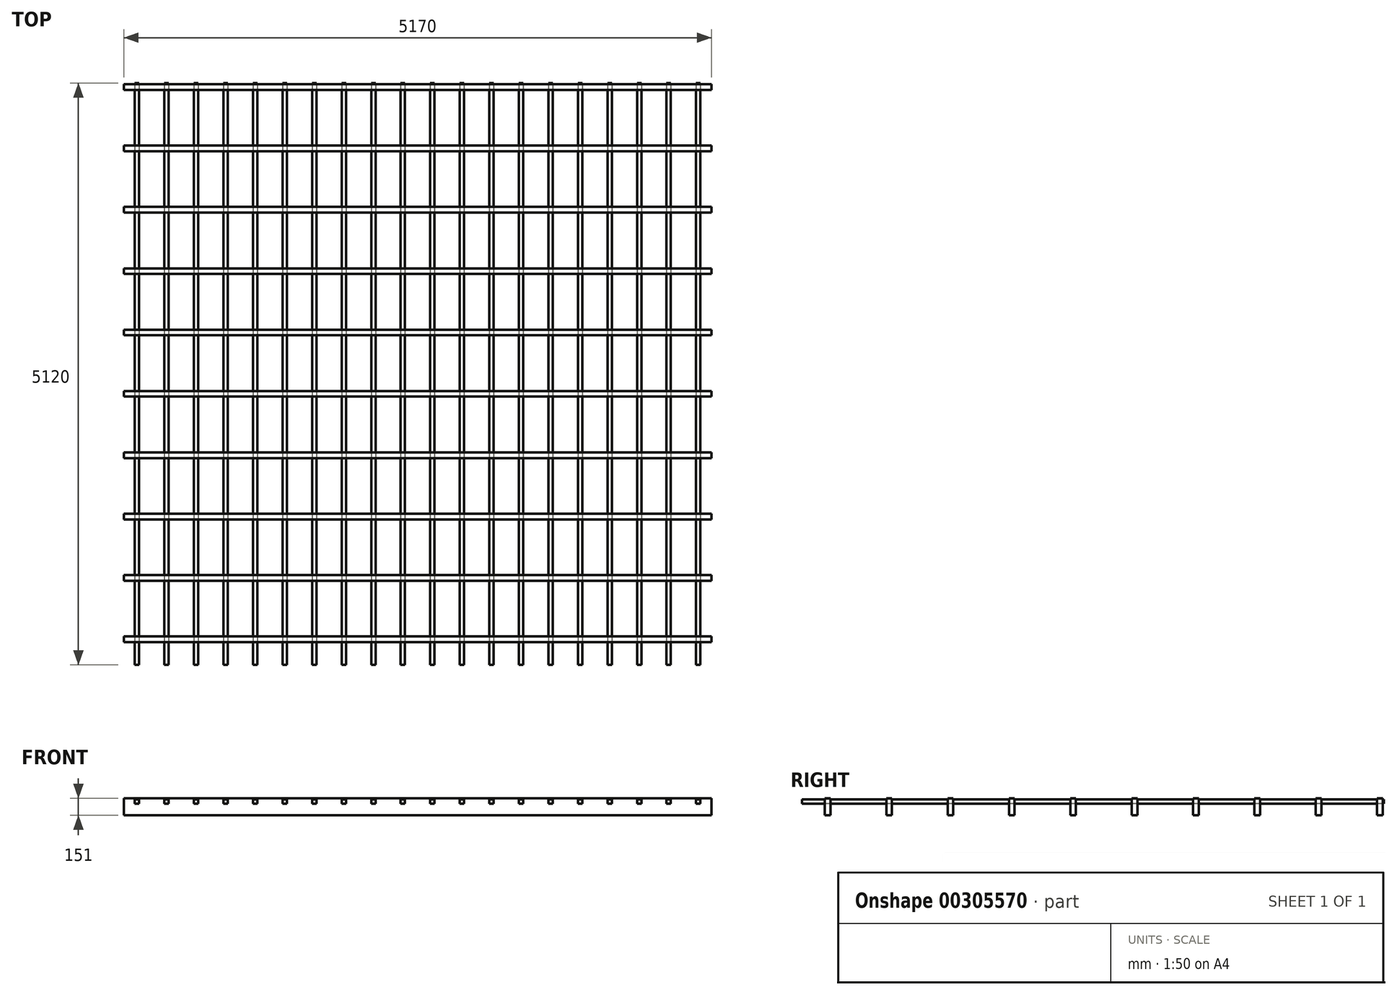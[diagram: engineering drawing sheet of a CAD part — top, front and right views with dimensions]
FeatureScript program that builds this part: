
annotation { "Feature Type Name" : "Feature", "Feature Type Description" : "" }
export const myFeature = defineFeature(function(context is Context, id is Id, definition is map)
    precondition{}
    {
        {
            var Q0;
            Q0=qCreatedBy(makeId("Top.planeOp"),FACE);
            var sketch = newSketch(context, id + "F0", { "sketchPlane" : qUnion([Q0])});
            skLineSegment(sketch, "E0.bottom", {"start": v(2585, -2460) * mm, "end": v(-2585, -2460) * mm});
            skLineSegment(sketch, "E0.top", {"start": v(2585, 2460) * mm, "end": v(-2585, 2460) * mm});
            skLineSegment(sketch, "E0.left", {"start": v(2585, -2460) * mm, "end": v(2585, 2460) * mm});
            skLineSegment(sketch, "E0.right", {"start": v(-2585, -2460) * mm, "end": v(-2585, 2460) * mm});
            skPoint(sketch, "E0.middle", {"position": v(0, 0) * mm});
            skLineSegment(sketch, "E1", {"start": v(-2585, -2410) * mm, "end": v(2585, -2410) * mm});
            skLineSegment(sketch, "E2.0.1.0", {"start": v(2585, -1920) * mm, "end": v(-2585, -1920) * mm});
            skLineSegment(sketch, "E2.0.1.1", {"start": v(-2585, -1870) * mm, "end": v(2585, -1870) * mm});
            skLineSegment(sketch, "E2.0.2.0", {"start": v(2585, -1380) * mm, "end": v(-2585, -1380) * mm});
            skLineSegment(sketch, "E2.0.2.1", {"start": v(-2585, -1330) * mm, "end": v(2585, -1330) * mm});
            skLineSegment(sketch, "E2.0.3.0", {"start": v(2585, -840) * mm, "end": v(-2585, -840) * mm});
            skLineSegment(sketch, "E2.0.3.1", {"start": v(-2585, -790) * mm, "end": v(2585, -790) * mm});
            skLineSegment(sketch, "E2.0.4.0", {"start": v(2585, -300) * mm, "end": v(-2585, -300) * mm});
            skLineSegment(sketch, "E2.0.4.1", {"start": v(-2585, -250) * mm, "end": v(2585, -250) * mm});
            skLineSegment(sketch, "E2.0.5.0", {"start": v(2585, 240) * mm, "end": v(-2585, 240) * mm});
            skLineSegment(sketch, "E2.0.5.1", {"start": v(-2585, 290) * mm, "end": v(2585, 290) * mm});
            skLineSegment(sketch, "E2.0.6.0", {"start": v(2585, 780) * mm, "end": v(-2585, 780) * mm});
            skLineSegment(sketch, "E2.0.6.1", {"start": v(-2585, 830) * mm, "end": v(2585, 830) * mm});
            skLineSegment(sketch, "E2.0.7.0", {"start": v(2585, 1320) * mm, "end": v(-2585, 1320) * mm});
            skLineSegment(sketch, "E2.0.7.1", {"start": v(-2585, 1370) * mm, "end": v(2585, 1370) * mm});
            skLineSegment(sketch, "E2.0.8.0", {"start": v(2585, 1860) * mm, "end": v(-2585, 1860) * mm});
            skLineSegment(sketch, "E2.0.8.1", {"start": v(-2585, 1910) * mm, "end": v(2585, 1910) * mm});
            skLineSegment(sketch, "E2.0.9.0", {"start": v(2585, 2400) * mm, "end": v(-2585, 2400) * mm});
            skLineSegment(sketch, "E2.0.9.1", {"start": v(-2585, 2450) * mm, "end": v(2585, 2450) * mm});
            skLineSegment(sketch, "E2.1.0.0", {"start": v(2610, -2460) * mm, "end": v(-2560, -2460) * mm});
            skLineSegment(sketch, "E2.1.0.1", {"start": v(-2560, -2410) * mm, "end": v(2610, -2410) * mm});
            skLineSegment(sketch, "E2.1.1.0", {"start": v(2610, -1920) * mm, "end": v(-2560, -1920) * mm});
            skLineSegment(sketch, "E2.1.1.1", {"start": v(-2560, -1870) * mm, "end": v(2610, -1870) * mm});
            skLineSegment(sketch, "E2.1.2.0", {"start": v(2610, -1380) * mm, "end": v(-2560, -1380) * mm});
            skLineSegment(sketch, "E2.1.2.1", {"start": v(-2560, -1330) * mm, "end": v(2610, -1330) * mm});
            skLineSegment(sketch, "E2.1.3.0", {"start": v(2610, -840) * mm, "end": v(-2560, -840) * mm});
            skLineSegment(sketch, "E2.1.3.1", {"start": v(-2560, -790) * mm, "end": v(2610, -790) * mm});
            skLineSegment(sketch, "E2.1.4.0", {"start": v(2610, -300) * mm, "end": v(-2560, -300) * mm});
            skLineSegment(sketch, "E2.1.4.1", {"start": v(-2560, -250) * mm, "end": v(2610, -250) * mm});
            skLineSegment(sketch, "E2.1.5.0", {"start": v(2610, 240) * mm, "end": v(-2560, 240) * mm});
            skLineSegment(sketch, "E2.1.5.1", {"start": v(-2560, 290) * mm, "end": v(2610, 290) * mm});
            skLineSegment(sketch, "E2.1.6.0", {"start": v(2610, 780) * mm, "end": v(-2560, 780) * mm});
            skLineSegment(sketch, "E2.1.6.1", {"start": v(-2560, 830) * mm, "end": v(2610, 830) * mm});
            skLineSegment(sketch, "E2.1.7.0", {"start": v(2610, 1320) * mm, "end": v(-2560, 1320) * mm});
            skLineSegment(sketch, "E2.1.7.1", {"start": v(-2560, 1370) * mm, "end": v(2610, 1370) * mm});
            skLineSegment(sketch, "E2.1.8.0", {"start": v(2610, 1860) * mm, "end": v(-2560, 1860) * mm});
            skLineSegment(sketch, "E2.1.8.1", {"start": v(-2560, 1910) * mm, "end": v(2610, 1910) * mm});
            skLineSegment(sketch, "E2.1.9.0", {"start": v(2610, 2400) * mm, "end": v(-2560, 2400) * mm});
            skLineSegment(sketch, "E2.1.9.1", {"start": v(-2560, 2450) * mm, "end": v(2610, 2450) * mm});
            skLineSegment(sketch, "E2.2.0.0", {"start": v(2635, -2460) * mm, "end": v(-2535, -2460) * mm});
            skLineSegment(sketch, "E2.2.0.1", {"start": v(-2535, -2410) * mm, "end": v(2635, -2410) * mm});
            skLineSegment(sketch, "E2.2.1.0", {"start": v(2635, -1920) * mm, "end": v(-2535, -1920) * mm});
            skLineSegment(sketch, "E2.2.1.1", {"start": v(-2535, -1870) * mm, "end": v(2635, -1870) * mm});
            skLineSegment(sketch, "E2.2.2.0", {"start": v(2635, -1380) * mm, "end": v(-2535, -1380) * mm});
            skLineSegment(sketch, "E2.2.2.1", {"start": v(-2535, -1330) * mm, "end": v(2635, -1330) * mm});
            skLineSegment(sketch, "E2.2.3.0", {"start": v(2635, -840) * mm, "end": v(-2535, -840) * mm});
            skLineSegment(sketch, "E2.2.3.1", {"start": v(-2535, -790) * mm, "end": v(2635, -790) * mm});
            skLineSegment(sketch, "E2.2.4.0", {"start": v(2635, -300) * mm, "end": v(-2535, -300) * mm});
            skLineSegment(sketch, "E2.2.4.1", {"start": v(-2535, -250) * mm, "end": v(2635, -250) * mm});
            skLineSegment(sketch, "E2.2.5.0", {"start": v(2635, 240) * mm, "end": v(-2535, 240) * mm});
            skLineSegment(sketch, "E2.2.5.1", {"start": v(-2535, 290) * mm, "end": v(2635, 290) * mm});
            skLineSegment(sketch, "E2.2.6.0", {"start": v(2635, 780) * mm, "end": v(-2535, 780) * mm});
            skLineSegment(sketch, "E2.2.6.1", {"start": v(-2535, 830) * mm, "end": v(2635, 830) * mm});
            skLineSegment(sketch, "E2.2.7.0", {"start": v(2635, 1320) * mm, "end": v(-2535, 1320) * mm});
            skLineSegment(sketch, "E2.2.7.1", {"start": v(-2535, 1370) * mm, "end": v(2635, 1370) * mm});
            skLineSegment(sketch, "E2.2.8.0", {"start": v(2635, 1860) * mm, "end": v(-2535, 1860) * mm});
            skLineSegment(sketch, "E2.2.8.1", {"start": v(-2535, 1910) * mm, "end": v(2635, 1910) * mm});
            skLineSegment(sketch, "E2.2.9.0", {"start": v(2635, 2400) * mm, "end": v(-2535, 2400) * mm});
            skLineSegment(sketch, "E2.2.9.1", {"start": v(-2535, 2450) * mm, "end": v(2635, 2450) * mm});
            skLineSegment(sketch, "E2.direction1", {"start": v(-2585, -2460) * mm, "end": v(-2560, -2460) * mm, "construction": true});
            skLineSegment(sketch, "E2.direction2", {"start": v(-2585, -2460) * mm, "end": v(-2585, -1920) * mm, "construction": true});
            skSolve(sketch);
        }
        {
            var Q0;
            {var subQ2=sQuery(id+"F0.wireOp",EDGE,"E0.bottom");Q0=makeQuery(id+"F0.imprint","IMPRINT",FACE,{"disambiguationData":[TD([[makeQuery(id+"F0.imprint","IMPRINT",EDGE,{"derivedFrom":subQ2}),-1.0]])]});}
            var Q1;
            {var subQ0=sQuery(id+"F0.wireOp",EDGE,"E2.0.1.0");Q1=makeQuery(id+"F0.imprint","IMPRINT",FACE,{"disambiguationData":[TD([[makeQuery(id+"F0.imprint","IMPRINT",EDGE,{"derivedFrom":subQ0}),-1.0]])]});}
            var Q2;
            {var subQ0=sQuery(id+"F0.wireOp",EDGE,"E2.0.2.0");Q2=makeQuery(id+"F0.imprint","IMPRINT",FACE,{"disambiguationData":[TD([[makeQuery(id+"F0.imprint","IMPRINT",EDGE,{"derivedFrom":subQ0}),-1.0]])]});}
            var Q3;
            {var subQ0=sQuery(id+"F0.wireOp",EDGE,"E2.0.3.0");Q3=makeQuery(id+"F0.imprint","IMPRINT",FACE,{"disambiguationData":[TD([[makeQuery(id+"F0.imprint","IMPRINT",EDGE,{"derivedFrom":subQ0}),-1.0]])]});}
            var Q4;
            {var subQ0=sQuery(id+"F0.wireOp",EDGE,"E2.0.4.0");Q4=makeQuery(id+"F0.imprint","IMPRINT",FACE,{"disambiguationData":[TD([[makeQuery(id+"F0.imprint","IMPRINT",EDGE,{"derivedFrom":subQ0}),-1.0]])]});}
            var Q5;
            {var subQ0=sQuery(id+"F0.wireOp",EDGE,"E2.0.5.0");Q5=makeQuery(id+"F0.imprint","IMPRINT",FACE,{"disambiguationData":[TD([[makeQuery(id+"F0.imprint","IMPRINT",EDGE,{"derivedFrom":subQ0}),-1.0]])]});}
            var Q6;
            {var subQ0=sQuery(id+"F0.wireOp",EDGE,"E2.0.6.0");Q6=makeQuery(id+"F0.imprint","IMPRINT",FACE,{"disambiguationData":[TD([[makeQuery(id+"F0.imprint","IMPRINT",EDGE,{"derivedFrom":subQ0}),-1.0]])]});}
            var Q7;
            {var subQ0=sQuery(id+"F0.wireOp",EDGE,"E2.0.7.0");Q7=makeQuery(id+"F0.imprint","IMPRINT",FACE,{"disambiguationData":[TD([[makeQuery(id+"F0.imprint","IMPRINT",EDGE,{"derivedFrom":subQ0}),-1.0]])]});}
            var Q8;
            {var subQ0=sQuery(id+"F0.wireOp",EDGE,"E2.0.8.0");Q8=makeQuery(id+"F0.imprint","IMPRINT",FACE,{"disambiguationData":[TD([[makeQuery(id+"F0.imprint","IMPRINT",EDGE,{"derivedFrom":subQ0}),-1.0]])]});}
            var Q9;
            {var subQ0=sQuery(id+"F0.wireOp",EDGE,"E2.0.9.0");Q9=makeQuery(id+"F0.imprint","IMPRINT",FACE,{"disambiguationData":[TD([[makeQuery(id+"F0.imprint","IMPRINT",EDGE,{"derivedFrom":subQ0}),-1.0]])]});}
            extrude(context, id + "F1", {"entities" : qUnion([Q0, Q1, Q2, Q3, Q4, Q5, Q6, Q7, Q8, Q9]), "depth" : 151 * mm});
        }
        {
            var Q0;
            Q0=makeQuery(id+"F1.opExtrude","SWEPT_FACE",FACE,{"disambiguationData":[OSD([sQuery(id+"F0.wireOp",EDGE,"E0.bottom"),sQuery(id+"F0.wireOp",EDGE,"E2.1.0.0"),sQuery(id+"F0.wireOp",EDGE,"E2.2.0.0")])]});
            var sketch = newSketch(context, id + "F2", { "sketchPlane" : qUnion([Q0])});
            skLineSegment(sketch, "E3.bottom", {"start": v(-2451, 103) * mm, "end": v(-2489, 103) * mm});
            skLineSegment(sketch, "E3.top", {"start": v(-2451, 141) * mm, "end": v(-2489, 141) * mm});
            skLineSegment(sketch, "E3.left", {"start": v(-2451, 103) * mm, "end": v(-2451, 141) * mm});
            skLineSegment(sketch, "E3.right", {"start": v(-2489, 103) * mm, "end": v(-2489, 141) * mm});
            skPoint(sketch, "E3.middle", {"position": v(-2470, 122) * mm});
            skLineSegment(sketch, "E4.1.0.0", {"start": v(-2229, 103) * mm, "end": v(-2229, 141) * mm});
            skLineSegment(sketch, "E4.1.0.1", {"start": v(-2191, 141) * mm, "end": v(-2229, 141) * mm});
            skLineSegment(sketch, "E4.1.0.2", {"start": v(-2191, 103) * mm, "end": v(-2191, 141) * mm});
            skLineSegment(sketch, "E4.1.0.3", {"start": v(-2191, 103) * mm, "end": v(-2229, 103) * mm});
            skLineSegment(sketch, "E4.2.0.0", {"start": v(-1969, 103) * mm, "end": v(-1969, 141) * mm});
            skLineSegment(sketch, "E4.2.0.1", {"start": v(-1931, 141) * mm, "end": v(-1969, 141) * mm});
            skLineSegment(sketch, "E4.2.0.2", {"start": v(-1931, 103) * mm, "end": v(-1931, 141) * mm});
            skLineSegment(sketch, "E4.2.0.3", {"start": v(-1931, 103) * mm, "end": v(-1969, 103) * mm});
            skLineSegment(sketch, "E4.3.0.0", {"start": v(-1709, 103) * mm, "end": v(-1709, 141) * mm});
            skLineSegment(sketch, "E4.3.0.1", {"start": v(-1671, 141) * mm, "end": v(-1709, 141) * mm});
            skLineSegment(sketch, "E4.3.0.2", {"start": v(-1671, 103) * mm, "end": v(-1671, 141) * mm});
            skLineSegment(sketch, "E4.3.0.3", {"start": v(-1671, 103) * mm, "end": v(-1709, 103) * mm});
            skLineSegment(sketch, "E4.4.0.0", {"start": v(-1449, 103) * mm, "end": v(-1449, 141) * mm});
            skLineSegment(sketch, "E4.4.0.1", {"start": v(-1411, 141) * mm, "end": v(-1449, 141) * mm});
            skLineSegment(sketch, "E4.4.0.2", {"start": v(-1411, 103) * mm, "end": v(-1411, 141) * mm});
            skLineSegment(sketch, "E4.4.0.3", {"start": v(-1411, 103) * mm, "end": v(-1449, 103) * mm});
            skLineSegment(sketch, "E4.5.0.0", {"start": v(-1189, 103) * mm, "end": v(-1189, 141) * mm});
            skLineSegment(sketch, "E4.5.0.1", {"start": v(-1151, 141) * mm, "end": v(-1189, 141) * mm});
            skLineSegment(sketch, "E4.5.0.2", {"start": v(-1151, 103) * mm, "end": v(-1151, 141) * mm});
            skLineSegment(sketch, "E4.5.0.3", {"start": v(-1151, 103) * mm, "end": v(-1189, 103) * mm});
            skLineSegment(sketch, "E4.6.0.0", {"start": v(-929, 103) * mm, "end": v(-929, 141) * mm});
            skLineSegment(sketch, "E4.6.0.1", {"start": v(-891, 141) * mm, "end": v(-929, 141) * mm});
            skLineSegment(sketch, "E4.6.0.2", {"start": v(-891, 103) * mm, "end": v(-891, 141) * mm});
            skLineSegment(sketch, "E4.6.0.3", {"start": v(-891, 103) * mm, "end": v(-929, 103) * mm});
            skLineSegment(sketch, "E4.7.0.0", {"start": v(-669, 103) * mm, "end": v(-669, 141) * mm});
            skLineSegment(sketch, "E4.7.0.1", {"start": v(-631, 141) * mm, "end": v(-669, 141) * mm});
            skLineSegment(sketch, "E4.7.0.2", {"start": v(-631, 103) * mm, "end": v(-631, 141) * mm});
            skLineSegment(sketch, "E4.7.0.3", {"start": v(-631, 103) * mm, "end": v(-669, 103) * mm});
            skLineSegment(sketch, "E4.8.0.0", {"start": v(-409, 103) * mm, "end": v(-409, 141) * mm});
            skLineSegment(sketch, "E4.8.0.1", {"start": v(-371, 141) * mm, "end": v(-409, 141) * mm});
            skLineSegment(sketch, "E4.8.0.2", {"start": v(-371, 103) * mm, "end": v(-371, 141) * mm});
            skLineSegment(sketch, "E4.8.0.3", {"start": v(-371, 103) * mm, "end": v(-409, 103) * mm});
            skLineSegment(sketch, "E4.9.0.0", {"start": v(-149, 103) * mm, "end": v(-149, 141) * mm});
            skLineSegment(sketch, "E4.9.0.1", {"start": v(-111, 141) * mm, "end": v(-149, 141) * mm});
            skLineSegment(sketch, "E4.9.0.2", {"start": v(-111, 103) * mm, "end": v(-111, 141) * mm});
            skLineSegment(sketch, "E4.9.0.3", {"start": v(-111, 103) * mm, "end": v(-149, 103) * mm});
            skLineSegment(sketch, "E4.10.0.0", {"start": v(111, 103) * mm, "end": v(111, 141) * mm});
            skLineSegment(sketch, "E4.10.0.1", {"start": v(149, 141) * mm, "end": v(111, 141) * mm});
            skLineSegment(sketch, "E4.10.0.2", {"start": v(149, 103) * mm, "end": v(149, 141) * mm});
            skLineSegment(sketch, "E4.10.0.3", {"start": v(149, 103) * mm, "end": v(111, 103) * mm});
            skLineSegment(sketch, "E4.11.0.0", {"start": v(371, 103) * mm, "end": v(371, 141) * mm});
            skLineSegment(sketch, "E4.11.0.1", {"start": v(409, 141) * mm, "end": v(371, 141) * mm});
            skLineSegment(sketch, "E4.11.0.2", {"start": v(409, 103) * mm, "end": v(409, 141) * mm});
            skLineSegment(sketch, "E4.11.0.3", {"start": v(409, 103) * mm, "end": v(371, 103) * mm});
            skLineSegment(sketch, "E4.12.0.0", {"start": v(631, 103) * mm, "end": v(631, 141) * mm});
            skLineSegment(sketch, "E4.12.0.1", {"start": v(669, 141) * mm, "end": v(631, 141) * mm});
            skLineSegment(sketch, "E4.12.0.2", {"start": v(669, 103) * mm, "end": v(669, 141) * mm});
            skLineSegment(sketch, "E4.12.0.3", {"start": v(669, 103) * mm, "end": v(631, 103) * mm});
            skLineSegment(sketch, "E4.13.0.0", {"start": v(891, 103) * mm, "end": v(891, 141) * mm});
            skLineSegment(sketch, "E4.13.0.1", {"start": v(929, 141) * mm, "end": v(891, 141) * mm});
            skLineSegment(sketch, "E4.13.0.2", {"start": v(929, 103) * mm, "end": v(929, 141) * mm});
            skLineSegment(sketch, "E4.13.0.3", {"start": v(929, 103) * mm, "end": v(891, 103) * mm});
            skLineSegment(sketch, "E4.14.0.0", {"start": v(1151, 103) * mm, "end": v(1151, 141) * mm});
            skLineSegment(sketch, "E4.14.0.1", {"start": v(1189, 141) * mm, "end": v(1151, 141) * mm});
            skLineSegment(sketch, "E4.14.0.2", {"start": v(1189, 103) * mm, "end": v(1189, 141) * mm});
            skLineSegment(sketch, "E4.14.0.3", {"start": v(1189, 103) * mm, "end": v(1151, 103) * mm});
            skLineSegment(sketch, "E4.15.0.0", {"start": v(1411, 103) * mm, "end": v(1411, 141) * mm});
            skLineSegment(sketch, "E4.15.0.1", {"start": v(1449, 141) * mm, "end": v(1411, 141) * mm});
            skLineSegment(sketch, "E4.15.0.2", {"start": v(1449, 103) * mm, "end": v(1449, 141) * mm});
            skLineSegment(sketch, "E4.15.0.3", {"start": v(1449, 103) * mm, "end": v(1411, 103) * mm});
            skLineSegment(sketch, "E4.16.0.0", {"start": v(1671, 103) * mm, "end": v(1671, 141) * mm});
            skLineSegment(sketch, "E4.16.0.1", {"start": v(1709, 141) * mm, "end": v(1671, 141) * mm});
            skLineSegment(sketch, "E4.16.0.2", {"start": v(1709, 103) * mm, "end": v(1709, 141) * mm});
            skLineSegment(sketch, "E4.16.0.3", {"start": v(1709, 103) * mm, "end": v(1671, 103) * mm});
            skLineSegment(sketch, "E4.17.0.0", {"start": v(1931, 103) * mm, "end": v(1931, 141) * mm});
            skLineSegment(sketch, "E4.17.0.1", {"start": v(1969, 141) * mm, "end": v(1931, 141) * mm});
            skLineSegment(sketch, "E4.17.0.2", {"start": v(1969, 103) * mm, "end": v(1969, 141) * mm});
            skLineSegment(sketch, "E4.17.0.3", {"start": v(1969, 103) * mm, "end": v(1931, 103) * mm});
            skLineSegment(sketch, "E4.18.0.0", {"start": v(2191, 103) * mm, "end": v(2191, 141) * mm});
            skLineSegment(sketch, "E4.18.0.1", {"start": v(2229, 141) * mm, "end": v(2191, 141) * mm});
            skLineSegment(sketch, "E4.18.0.2", {"start": v(2229, 103) * mm, "end": v(2229, 141) * mm});
            skLineSegment(sketch, "E4.18.0.3", {"start": v(2229, 103) * mm, "end": v(2191, 103) * mm});
            skLineSegment(sketch, "E4.direction1", {"start": v(-2489, 103) * mm, "end": v(-2229, 103) * mm, "construction": true});
            skLineSegment(sketch, "E5.0.19.0", {"start": v(2451, 103) * mm, "end": v(2451, 141) * mm});
            skLineSegment(sketch, "E5.3.19.0", {"start": v(2489, 141) * mm, "end": v(2451, 141) * mm});
            skLineSegment(sketch, "E5.6.19.0", {"start": v(2489, 103) * mm, "end": v(2489, 141) * mm});
            skLineSegment(sketch, "E5.9.19.0", {"start": v(2489, 103) * mm, "end": v(2451, 103) * mm});
            skSolve(sketch);
        }
        {
            var Q0;
            Q0=makeQuery(id+"F2.imprint","IMPRINT",FACE,{"disambiguationData":[TD([[makeQuery(id+"F2.imprint","IMPRINT",EDGE,{"derivedFrom":sQuery(id+"F2.wireOp",EDGE,"E5.0.19.0")}),-1.0]])]});
            var Q1;
            Q1=makeQuery(id+"F2.imprint","IMPRINT",FACE,{"disambiguationData":[TD([[makeQuery(id+"F2.imprint","IMPRINT",EDGE,{"derivedFrom":sQuery(id+"F2.wireOp",EDGE,"E4.18.0.0")}),-1.0]])]});
            var Q2;
            Q2=makeQuery(id+"F2.imprint","IMPRINT",FACE,{"disambiguationData":[TD([[makeQuery(id+"F2.imprint","IMPRINT",EDGE,{"derivedFrom":sQuery(id+"F2.wireOp",EDGE,"E4.17.0.0")}),-1.0]])]});
            var Q3;
            Q3=makeQuery(id+"F2.imprint","IMPRINT",FACE,{"disambiguationData":[TD([[makeQuery(id+"F2.imprint","IMPRINT",EDGE,{"derivedFrom":sQuery(id+"F2.wireOp",EDGE,"E4.16.0.0")}),-1.0]])]});
            var Q4;
            Q4=makeQuery(id+"F2.imprint","IMPRINT",FACE,{"disambiguationData":[TD([[makeQuery(id+"F2.imprint","IMPRINT",EDGE,{"derivedFrom":sQuery(id+"F2.wireOp",EDGE,"E4.15.0.0")}),-1.0]])]});
            var Q5;
            Q5=makeQuery(id+"F2.imprint","IMPRINT",FACE,{"disambiguationData":[TD([[makeQuery(id+"F2.imprint","IMPRINT",EDGE,{"derivedFrom":sQuery(id+"F2.wireOp",EDGE,"E4.14.0.0")}),-1.0]])]});
            var Q6;
            Q6=makeQuery(id+"F2.imprint","IMPRINT",FACE,{"disambiguationData":[TD([[makeQuery(id+"F2.imprint","IMPRINT",EDGE,{"derivedFrom":sQuery(id+"F2.wireOp",EDGE,"E4.13.0.0")}),-1.0]])]});
            var Q7;
            Q7=makeQuery(id+"F2.imprint","IMPRINT",FACE,{"disambiguationData":[TD([[makeQuery(id+"F2.imprint","IMPRINT",EDGE,{"derivedFrom":sQuery(id+"F2.wireOp",EDGE,"E4.12.0.0")}),-1.0]])]});
            var Q8;
            Q8=makeQuery(id+"F2.imprint","IMPRINT",FACE,{"disambiguationData":[TD([[makeQuery(id+"F2.imprint","IMPRINT",EDGE,{"derivedFrom":sQuery(id+"F2.wireOp",EDGE,"E4.11.0.0")}),-1.0]])]});
            var Q9;
            Q9=makeQuery(id+"F2.imprint","IMPRINT",FACE,{"disambiguationData":[TD([[makeQuery(id+"F2.imprint","IMPRINT",EDGE,{"derivedFrom":sQuery(id+"F2.wireOp",EDGE,"E4.10.0.0")}),-1.0]])]});
            var Q10;
            Q10=makeQuery(id+"F2.imprint","IMPRINT",FACE,{"disambiguationData":[TD([[makeQuery(id+"F2.imprint","IMPRINT",EDGE,{"derivedFrom":sQuery(id+"F2.wireOp",EDGE,"E4.9.0.0")}),-1.0]])]});
            var Q11;
            Q11=makeQuery(id+"F2.imprint","IMPRINT",FACE,{"disambiguationData":[TD([[makeQuery(id+"F2.imprint","IMPRINT",EDGE,{"derivedFrom":sQuery(id+"F2.wireOp",EDGE,"E4.8.0.0")}),-1.0]])]});
            var Q12;
            Q12=makeQuery(id+"F2.imprint","IMPRINT",FACE,{"disambiguationData":[TD([[makeQuery(id+"F2.imprint","IMPRINT",EDGE,{"derivedFrom":sQuery(id+"F2.wireOp",EDGE,"E4.7.0.0")}),-1.0]])]});
            var Q13;
            Q13=makeQuery(id+"F2.imprint","IMPRINT",FACE,{"disambiguationData":[TD([[makeQuery(id+"F2.imprint","IMPRINT",EDGE,{"derivedFrom":sQuery(id+"F2.wireOp",EDGE,"E4.6.0.0")}),-1.0]])]});
            var Q14;
            Q14=makeQuery(id+"F2.imprint","IMPRINT",FACE,{"disambiguationData":[TD([[makeQuery(id+"F2.imprint","IMPRINT",EDGE,{"derivedFrom":sQuery(id+"F2.wireOp",EDGE,"E4.5.0.0")}),-1.0]])]});
            var Q15;
            Q15=makeQuery(id+"F2.imprint","IMPRINT",FACE,{"disambiguationData":[TD([[makeQuery(id+"F2.imprint","IMPRINT",EDGE,{"derivedFrom":sQuery(id+"F2.wireOp",EDGE,"E4.4.0.0")}),-1.0]])]});
            var Q16;
            Q16=makeQuery(id+"F2.imprint","IMPRINT",FACE,{"disambiguationData":[TD([[makeQuery(id+"F2.imprint","IMPRINT",EDGE,{"derivedFrom":sQuery(id+"F2.wireOp",EDGE,"E4.3.0.0")}),-1.0]])]});
            var Q17;
            Q17=makeQuery(id+"F2.imprint","IMPRINT",FACE,{"disambiguationData":[TD([[makeQuery(id+"F2.imprint","IMPRINT",EDGE,{"derivedFrom":sQuery(id+"F2.wireOp",EDGE,"E4.2.0.0")}),-1.0]])]});
            var Q18;
            Q18=makeQuery(id+"F2.imprint","IMPRINT",FACE,{"disambiguationData":[TD([[makeQuery(id+"F2.imprint","IMPRINT",EDGE,{"derivedFrom":sQuery(id+"F2.wireOp",EDGE,"E4.1.0.0")}),-1.0]])]});
            var Q19;
            Q19=makeQuery(id+"F2.imprint","IMPRINT",FACE,{"disambiguationData":[TD([[makeQuery(id+"F2.imprint","IMPRINT",EDGE,{"derivedFrom":sQuery(id+"F2.wireOp",EDGE,"E3.bottom")}),-1.0]])]});
            extrude(context, id + "F3", {"entities" : qUnion([Q0, Q1, Q2, Q3, Q4, Q5, Q6, Q7, Q8, Q9, Q10, Q11, Q12, Q13, Q14, Q15, Q16, Q17, Q18, Q19]), "oppositeDirection" : true, "depth" : 4920 * mm, "hasSecondDirection" : true, "secondDirectionOppositeDirection" : false, "secondDirectionDepth" : 200 * mm});
        }
    });
